# Revit family: Valve_Trim-DXV-Percy-D35105537_Series
name_source: partatom
category: Plumbing Fixtures
revit_build: Autodesk Revit 2014 (Build: 20130308_1515(x64)
units: mm (PartAtom-declared; Revit-internal decimal feet)

## types (2) — shared parameters
ADA Compliant = Yes
Assembly Code = D2010710
CW Connection = Yes
CWFU = 3
Cold Water Connection Diameter = 3/4"
Cold Water Connection Radius = 3/8"
D35005532.191 - Thermostatic Rough Valve with 2 Volume Controls = Yes
D35005533.191 - Thermostatic Rough Valve with 2-Way Diverter (Discrete Functions) = No
D35005533S.191 - Thermostatic Rough Valve with 2-Way Diverter (Shared Functions) = Yes
Default Elevation = 44"
Description = Percy 2-Handle Thermostatic Valve Trim
HW Connection = Yes
HWFU = 3
Height = 11 3/4"
Hot Water Connection Diameter = 1"
Hot Water Connection Radius = 3/8"
Installation Type = Wall Mounted
Length = 2 1/16"
Manufacturer = DXV
Price = Prices may vary. Please consult Manufacturer Representative for most up-to-date price list.
Tempered Water Connection Diameter = 1/2"
Tempered Water Connection Radius = 1/4"
URL = www.dxv.com
Valve Length = 3"
Vent Connection = No
WFU = 4
Warranty Documentation Link = https://www.dxv.com
Waste Connection = No
Width = 3 3/4"

## per-type parameters (varying)
| type | Finish | Material |
| D35105537.100 | Cast Brass-DXV-100-Polished Chrome | Cast Brass-DXV-100-Polished Chrome |
| D35105537.144 | Cast Brass-DXV-144-Brushed Nickel | Cast Brass-DXV-144-Brushed Nickel |

note: column(s) folded — value = type name in every type: Model

## geometry (parser evidence)
native form markers: Sweep x3
no freeform markers — native parametric forms only
